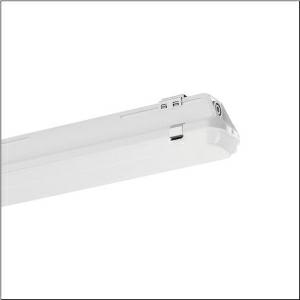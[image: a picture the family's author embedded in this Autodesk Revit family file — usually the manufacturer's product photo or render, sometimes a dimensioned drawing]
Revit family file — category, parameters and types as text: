
# Revit family: monsun_r__21_51fb10dp360c_4dea
name_source: partatom
category: Lighting Fixtures
units: mm (PartAtom-declared; Revit-internal decimal feet)

## family parameters
Cut with Voids When Loaded = No
Host = Face
Light Source = No
Part Type = Normal
Room Calculation Point = No
Round Connector Dimension = Use Diameter
Shared = No

## types (1)
- --- (1 x LED, 6060 lm, 34.9 W, 3000K)
    Apparent Load = 35 VA
    CIE Flux Codes = 47 77 93 94 100
    Color Rendering = 80
    Color Temperature = 3000K
    Default Elevation = 1800 mm
    Description = Monsun® 21, damp-proof luminaire, chain hanger, primary optical cover: enclosure, of PMMA, light emission: direct distribution, primary light characteristic: symmetric, installation type: suspended mounting, surface-mounted, horizontal mounting, vertical mounting, LED, rated luminous flux: 6.060lm, luminous efficacy: 174lm/W, light colour: 830, colour temperature: 3000K, control gear: DALI 2, with terminal, 5-pole, max. 2.5mm², mains connection: 220..240V, AC, 50/60Hz, rated input power: 35W, housing, of glass-fibre reinforced polyester, uncoated, bright grey, incl. chain hanger, length: 1.590mm, width: 90mm, height: 88mm, clip for enclosure, of stainless steel (V2A), ceiling mounting element, of stainless steel (V2A), chain hanger, of stainless steel (V2A), protection rating (complete): IP66, insulation class (complete): insulation class I (protective earthing), certification: CE, ENEC, VDE, UKCA, protection symbol: D, impact resistance: IK04, permissible operating ambient temperature: -25..+35°C, standard: EN 50419, EN 60598-2-1, corresponds to IFS (International Featured Standards) requirements for safety and quality in the food industry, for indoor or canopied outdoor use, no direct snow, no direct sun, no direct rain, LABS conformity tested according to VDMA 24364:2018-05, contact your sales advisor before using the luminaires in applications with unclear chemical exposure, large temperature fluctuations or condensation-forming humidity, packaging unit: 1 piece
    Height = 89 mm
    Lamp = 1 x LED
    Lamp Light Flux = 6060 lm
    Lamp Power = 34.9 W
    Lamp count = 1
    Length = 1590 mm
    Luminous efficacy = 174 lm/W
    Manufacturer = Siteco
    ModVariant = No
    Model = 51FB10DP360C
    Mounting Place = Ceiling
    Mounting Type = Surface mounted
    Number of Poles = 1
    OnlyDefault = Yes
    Power Factor = 1
    Product Name = Monsun® 21
    Product group = damp-proof luminaire
    ProductGroupID = 300
    Protection Class = Protection class I
    Protection Degree = IP 66
    RLX_Detail_Level = 1
    RLX_Emergency_Light_Flux = 0 lm
    RLX_Emergency_Type = 0
    RLX_Emergency_Type_DB = No
    RlxData = <blob elided: 92361 chars, md5=88e55575>
    Socket = socket
    Standby Power = 0 W
    System Light Flux = 6060 lm
    System Power = 35 W
    Type Comments = factory setting: luminous flux: 100 % | dim-lin: 254 | 245 mA
    Type Image = l_1319656.jpg
    URL = http://relux.com
    VarID = @adj_032006
    Voltage = 0 V
    Weight = 0.00 kg
    Width = 90 mm

## geometry (parser evidence)
native form markers: Blend x4, Sweep x14
no freeform markers — native parametric forms only
